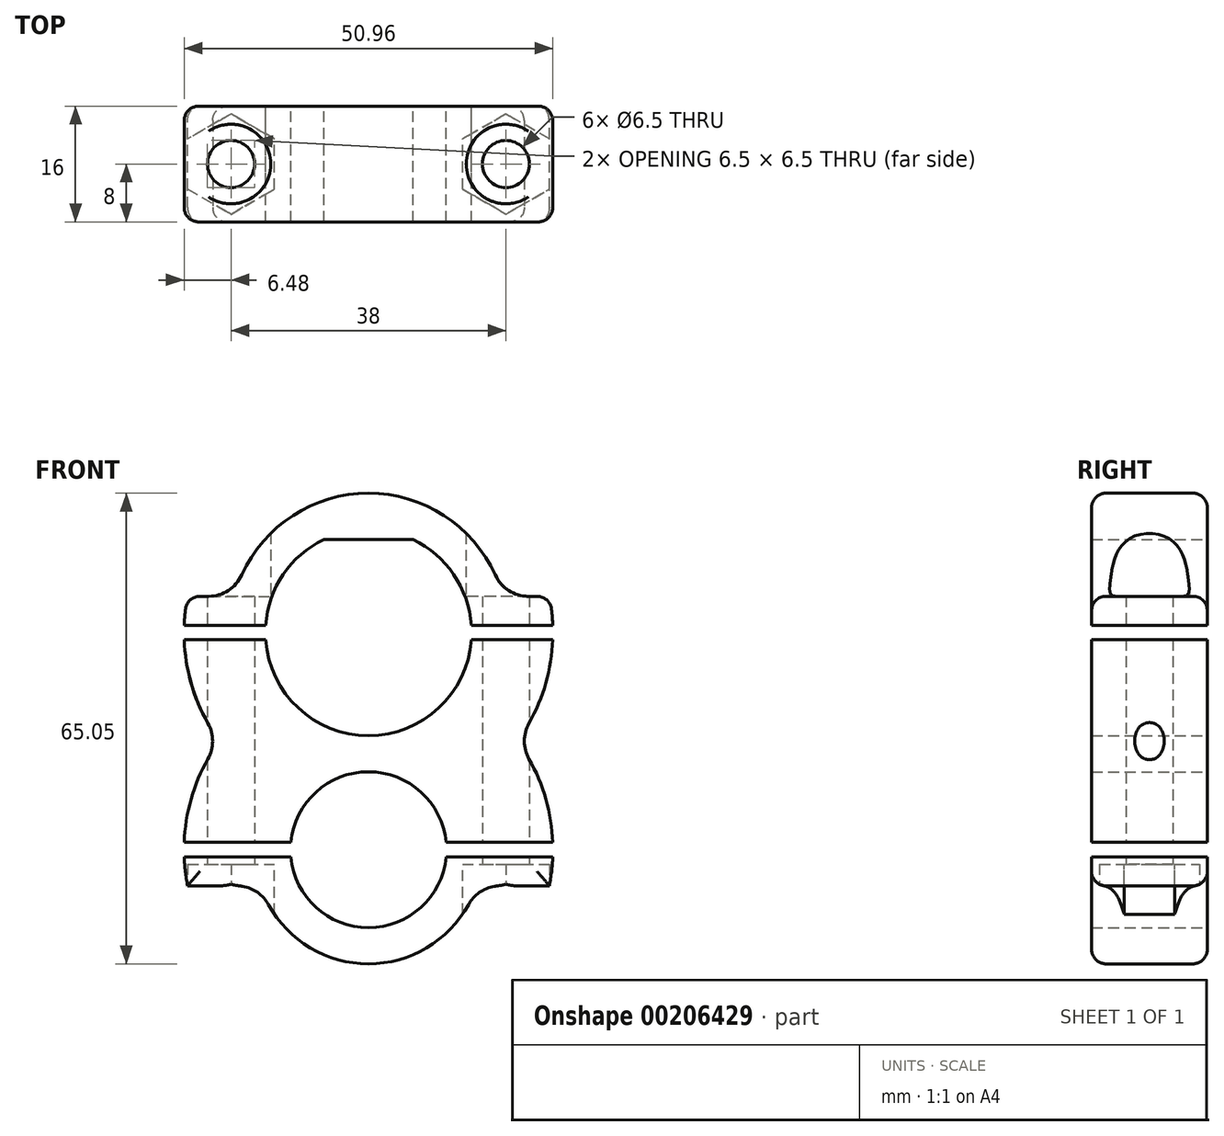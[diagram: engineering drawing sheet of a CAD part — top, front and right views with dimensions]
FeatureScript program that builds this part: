
annotation { "Feature Type Name" : "Feature", "Feature Type Description" : "" }
export const myFeature = defineFeature(function(context is Context, id is Id, definition is map)
    precondition{}
    {
        {
            var Q0;
            Q0=qCreatedBy(makeId("Front.planeOp"),FACE);
            var sketch = newSketch(context, id + "F0", { "sketchPlane" : qUnion([Q0])});
            skArc(sketch, "E0", {"start": v(-6.16, 12.85) * mm, "mid": v(-11.78, 8.01) * mm, "end": v(-14.21, 1) * mm});
            skArc(sketch, "E1", {"start": v(10.73, -29.02) * mm, "mid": v(0, -19.25) * mm, "end": v(-10.73, -29.02) * mm});
            skLineSegment(sketch, "E2", {"start": v(-6.16, 12.85) * mm, "end": v(6.16, 12.85) * mm});
            skLineSegment(sketch, "E3", {"start": v(-25, -35.02) * mm, "end": v(-14.96, -35.02) * mm});
            skLineSegment(sketch, "E4", {"start": v(-25, -25.02) * mm, "end": v(25, -25.02) * mm, "construction": true});
            skLineSegment(sketch, "E5", {"start": v(-25, -5) * mm, "end": v(25, -5) * mm, "construction": true});
            skLineSegment(sketch, "E6", {"start": v(-25, 5) * mm, "end": v(-18.59, 5) * mm});
            skArc(sketch, "E7", {"start": v(-25, 5) * mm, "mid": v(-25.32, 3) * mm, "end": v(-25.48, 1) * mm});
            skArc(sketch, "E8", {"start": v(25, -35.02) * mm, "mid": v(25.32, -33.03) * mm, "end": v(25.48, -31.03) * mm});
            skArc(sketch, "E9", {"start": v(20.6, -15.01) * mm, "mid": v(24.08, -8.37) * mm, "end": v(25.48, -1) * mm});
            skArc(sketch, "E10", {"start": v(-20.6, -15.01) * mm, "mid": v(-24.08, -21.66) * mm, "end": v(-25.48, -29.02) * mm});
            skLineSegment(sketch, "E11", {"start": v(-18.59, 5) * mm, "end": v(18.59, 5) * mm, "construction": true});
            skLineSegment(sketch, "E12", {"start": v(18.59, 5) * mm, "end": v(25, 5) * mm});
            skLineSegment(sketch, "E13", {"start": v(14.96, -35.02) * mm, "end": v(25, -35.02) * mm});
            skLineSegment(sketch, "E14", {"start": v(-14.96, -35.02) * mm, "end": v(14.96, -35.02) * mm, "construction": true});
            skArc(sketch, "E15", {"start": v(18.59, 5) * mm, "mid": v(0, 19.25) * mm, "end": v(-18.59, 5) * mm});
            skArc(sketch, "E16", {"start": v(-14.96, -35.02) * mm, "mid": v(0, -45.8) * mm, "end": v(14.96, -35.02) * mm});
            skLineSegment(sketch, "E17", {"start": v(-25.48, -31.03) * mm, "end": v(-10.73, -31.03) * mm});
            skLineSegment(sketch, "E18", {"start": v(-25.48, -29.02) * mm, "end": v(-10.73, -29.02) * mm});
            skLineSegment(sketch, "E19", {"start": v(-25.48, 1) * mm, "end": v(-14.21, 1) * mm});
            skLineSegment(sketch, "E20", {"start": v(25.48, -1) * mm, "end": v(14.21, -1) * mm});
            skLineSegment(sketch, "E21.trimOffspring", {"start": v(14.21, 1) * mm, "end": v(25.48, 1) * mm});
            skLineSegment(sketch, "E22.trimOffspring", {"start": v(-14.21, -1) * mm, "end": v(-25.48, -1) * mm});
            skLineSegment(sketch, "E23.trimOffspring", {"start": v(10.73, -29.02) * mm, "end": v(25.48, -29.02) * mm});
            skLineSegment(sketch, "E24.trimOffspring", {"start": v(10.73, -31.03) * mm, "end": v(25.48, -31.03) * mm});
            skArc(sketch, "E25.trimOffspring", {"start": v(-25.48, -1) * mm, "mid": v(-24.08, -8.37) * mm, "end": v(-20.6, -15.01) * mm});
            skArc(sketch, "E26.trimOffspring", {"start": v(25.48, 1) * mm, "mid": v(25.32, 3) * mm, "end": v(25, 5) * mm});
            skArc(sketch, "E27.trimOffspring", {"start": v(-25.48, -31.03) * mm, "mid": v(-25.32, -33.03) * mm, "end": v(-25, -35.02) * mm});
            skArc(sketch, "E28.trimOffspring", {"start": v(25.48, -29.02) * mm, "mid": v(24.08, -21.66) * mm, "end": v(20.6, -15.01) * mm});
            skArc(sketch, "E29.trimOffspring", {"start": v(-10.73, -31.03) * mm, "mid": v(0, -40.8) * mm, "end": v(10.73, -31.03) * mm});
            skArc(sketch, "E30.trimOffspring", {"start": v(-14.21, -1) * mm, "mid": v(0, -14.25) * mm, "end": v(14.21, -1) * mm});
            skArc(sketch, "E31.trimOffspring", {"start": v(14.21, 1) * mm, "mid": v(11.78, 8.01) * mm, "end": v(6.16, 12.85) * mm});
            skSolve(sketch);
        }
        {
            var Q0;
            Q0 = qSketchRegion(id + "F0", true);
            extrude(context, id + "F1", {"entities" : qUnion([Q0]), "endBound" : BoundingType.SYMMETRIC, "depth" : 16 * mm});
        }
        {
            var Q0;
            Q0=makeQuery(id+"F1.opExtrude","SWEPT_FACE",FACE,{"disambiguationData":[OSD([sQuery(id+"F0.wireOp",EDGE,"E3")])]});
            var sketch = newSketch(context, id + "F2", { "sketchPlane" : qUnion([Q0])});
            skCircle(sketch, "E32.cCircle", {"center": v(-19, 0) * mm, "radius": 6 * mm, "construction": true});
            skLineSegment(sketch, "E32.0", {"start": v(-19, 6.93) * mm, "end": v(-13, 3.46) * mm});
            skLineSegment(sketch, "E32.1", {"start": v(-13, 3.46) * mm, "end": v(-13, -3.46) * mm});
            skLineSegment(sketch, "E32.2", {"start": v(-13, -3.46) * mm, "end": v(-19, -6.93) * mm});
            skLineSegment(sketch, "E32.3", {"start": v(-19, -6.93) * mm, "end": v(-25, -3.46) * mm});
            skLineSegment(sketch, "E32.4", {"start": v(-25, -3.46) * mm, "end": v(-25, 3.46) * mm});
            skLineSegment(sketch, "E32.5", {"start": v(-25, 3.46) * mm, "end": v(-19, 6.93) * mm});
            skPoint(sketch, "E32.0.midPoint", {"position": v(-16, 5.2) * mm});
            skCircle(sketch, "E33.cCircle", {"center": v(19, 0) * mm, "radius": 6 * mm, "construction": true});
            skLineSegment(sketch, "E33.0", {"start": v(19, 6.93) * mm, "end": v(25, 3.46) * mm});
            skLineSegment(sketch, "E33.1", {"start": v(25, 3.46) * mm, "end": v(25, -3.46) * mm});
            skLineSegment(sketch, "E33.2", {"start": v(25, -3.46) * mm, "end": v(19, -6.93) * mm});
            skLineSegment(sketch, "E33.3", {"start": v(19, -6.93) * mm, "end": v(13, -3.46) * mm});
            skLineSegment(sketch, "E33.4", {"start": v(13, -3.46) * mm, "end": v(13, 3.46) * mm});
            skLineSegment(sketch, "E33.5", {"start": v(13, 3.46) * mm, "end": v(19, 6.93) * mm});
            skPoint(sketch, "E33.0.midPoint", {"position": v(22, 5.2) * mm});
            skCircle(sketch, "E34", {"center": v(-19, 0) * mm, "radius": 3.25 * mm});
            skCircle(sketch, "E35", {"center": v(19, 0) * mm, "radius": 3.25 * mm});
            skSolve(sketch);
        }
        {
            var Q0;
            {var subQ0=sQuery(id+"F2.wireOp",EDGE,"E34");var subQ1=makeQuery(id+"F1.opExtrude","SWEPT_EDGE",EDGE,{"disambiguationData":[OSD([sQuery(id+"F0.wireOp",EDGE,"E3"),sQuery(id+"F0.wireOp",EDGE,"E16")])]});var subQ2=makeQuery(id+"F2.imprint","INTERSECT",VERTEX,{"disambiguationData":[OD(0.0)],"derivedFrom":[subQ1,subQ0]});Q0=makeQuery(id+"F2.imprint","IMPRINT",FACE,{"disambiguationData":[TD([[makeQuery(id+"F2.imprint","IMPRINT",EDGE,{"disambiguationData":[TD([[subQ2,-1.0]])],"derivedFrom":subQ0}),1.0]])]});}
            var Q1;
            Q1=makeQuery(id+"F2.imprint","IMPRINT",FACE,{"disambiguationData":[TD([[makeQuery(id+"F2.imprint","IMPRINT",EDGE,{"derivedFrom":sQuery(id+"F2.wireOp",EDGE,"E35")}),1.0]])]});
            extrude(context, id + "F3", {"entities" : qUnion([Q0, Q1]), "operationType" : NewBodyOperationType.REMOVE, "endBound" : BoundingType.THROUGH_ALL, "oppositeDirection" : true, "depth" : 25 * mm});
        }
        {
            var Q0;
            Q0 = qSketchRegion(id + "F2", true);
            extrude(context, id + "F4", {"entities" : qUnion([Q0]), "operationType" : NewBodyOperationType.REMOVE, "depth" : 25 * mm});
        }
        {
            var Q0;
            Q0 = qSketchRegion(id + "F2", true);
            extrude(context, id + "F5", {"entities" : qUnion([Q0]), "operationType" : NewBodyOperationType.REMOVE, "oppositeDirection" : true, "depth" : 3 * mm});
        }
        {
            var Q0;
            Q0=makeQuery(id+"F1.opExtrude","SWEPT_FACE",FACE,{"disambiguationData":[OSD([sQuery(id+"F0.wireOp",EDGE,"E6")])]});
            var sketch = newSketch(context, id + "F6", { "sketchPlane" : qUnion([Q0])});
            skCircle(sketch, "E36", {"center": v(-19, 0) * mm, "radius": 5.5 * mm});
            skCircle(sketch, "E37", {"center": v(19, 0) * mm, "radius": 5.5 * mm});
            skSolve(sketch);
        }
        {
            var Q0;
            Q0 = qSketchRegion(id + "F6", true);
            extrude(context, id + "F7", {"entities" : qUnion([Q0]), "operationType" : NewBodyOperationType.REMOVE, "depth" : 25 * mm});
        }
        {
            var Q0;
            {var subQ0=sQuery(id+"F0.wireOp",EDGE,"E15");var subQ1=sQuery(id+"F0.wireOp",EDGE,"E6");Q0=makeQuery(id+"F3.boolean.opBoolean","SPLIT",EDGE,{"disambiguationData":[TD([makeQuery(id+"F1.opExtrude","CAP_FACE",FACE,{"disambiguationData":[OSD([sQuery(id+"F0.wireOp",EDGE,"E0"),sQuery(id+"F0.wireOp",EDGE,"E2"),subQ1,sQuery(id+"F0.wireOp",EDGE,"E7"),sQuery(id+"F0.wireOp",EDGE,"E12"),subQ0,sQuery(id+"F0.wireOp",EDGE,"E19"),sQuery(id+"F0.wireOp",EDGE,"E21.trimOffspring"),sQuery(id+"F0.wireOp",EDGE,"E26.trimOffspring"),sQuery(id+"F0.wireOp",EDGE,"E31.trimOffspring")])],"isStart":false})])],"derivedFrom":makeQuery(id+"F1.opExtrude","SWEPT_EDGE",EDGE,{"disambiguationData":[OSD([subQ1,subQ0])]})});}
            var Q1;
            {var subQ0=sQuery(id+"F0.wireOp",EDGE,"E15");var subQ1=sQuery(id+"F0.wireOp",EDGE,"E6");Q1=makeQuery(id+"F3.boolean.opBoolean","SPLIT",EDGE,{"disambiguationData":[TD([makeQuery(id+"F1.opExtrude","CAP_FACE",FACE,{"disambiguationData":[OSD([sQuery(id+"F0.wireOp",EDGE,"E0"),sQuery(id+"F0.wireOp",EDGE,"E2"),subQ1,sQuery(id+"F0.wireOp",EDGE,"E7"),sQuery(id+"F0.wireOp",EDGE,"E12"),subQ0,sQuery(id+"F0.wireOp",EDGE,"E19"),sQuery(id+"F0.wireOp",EDGE,"E21.trimOffspring"),sQuery(id+"F0.wireOp",EDGE,"E26.trimOffspring"),sQuery(id+"F0.wireOp",EDGE,"E31.trimOffspring")])],"isStart":true})])],"derivedFrom":makeQuery(id+"F1.opExtrude","SWEPT_EDGE",EDGE,{"disambiguationData":[OSD([subQ1,subQ0])]})});}
            var Q2;
            {var subQ0=sQuery(id+"F0.wireOp",EDGE,"E15");var subQ1=sQuery(id+"F0.wireOp",EDGE,"E12");Q2=makeQuery(id+"F3.boolean.opBoolean","SPLIT",EDGE,{"disambiguationData":[TD([makeQuery(id+"F1.opExtrude","CAP_FACE",FACE,{"disambiguationData":[OSD([sQuery(id+"F0.wireOp",EDGE,"E0"),sQuery(id+"F0.wireOp",EDGE,"E2"),sQuery(id+"F0.wireOp",EDGE,"E6"),sQuery(id+"F0.wireOp",EDGE,"E7"),subQ1,subQ0,sQuery(id+"F0.wireOp",EDGE,"E19"),sQuery(id+"F0.wireOp",EDGE,"E21.trimOffspring"),sQuery(id+"F0.wireOp",EDGE,"E26.trimOffspring"),sQuery(id+"F0.wireOp",EDGE,"E31.trimOffspring")])],"isStart":false})])],"derivedFrom":makeQuery(id+"F1.opExtrude","SWEPT_EDGE",EDGE,{"disambiguationData":[OSD([subQ1,subQ0])]})});}
            var Q3;
            {var subQ0=sQuery(id+"F0.wireOp",EDGE,"E15");var subQ1=sQuery(id+"F0.wireOp",EDGE,"E12");Q3=makeQuery(id+"F3.boolean.opBoolean","SPLIT",EDGE,{"disambiguationData":[TD([makeQuery(id+"F1.opExtrude","CAP_FACE",FACE,{"disambiguationData":[OSD([sQuery(id+"F0.wireOp",EDGE,"E0"),sQuery(id+"F0.wireOp",EDGE,"E2"),sQuery(id+"F0.wireOp",EDGE,"E6"),sQuery(id+"F0.wireOp",EDGE,"E7"),subQ1,subQ0,sQuery(id+"F0.wireOp",EDGE,"E19"),sQuery(id+"F0.wireOp",EDGE,"E21.trimOffspring"),sQuery(id+"F0.wireOp",EDGE,"E26.trimOffspring"),sQuery(id+"F0.wireOp",EDGE,"E31.trimOffspring")])],"isStart":true})])],"derivedFrom":makeQuery(id+"F1.opExtrude","SWEPT_EDGE",EDGE,{"disambiguationData":[OSD([subQ1,subQ0])]})});}
            var Q4;
            {var subQ0=sQuery(id+"F2.wireOp",EDGE,"E33.5");var subQ1=sQuery(id+"F0.wireOp",EDGE,"E13");var subQ2=sQuery(id+"F0.wireOp",EDGE,"E16");Q4=makeQuery(id+"F4.boolean.opBoolean","SPLIT",EDGE,{"disambiguationData":[TD([makeQuery(id+"F4.opExtrude","SWEPT_FACE",FACE,{"disambiguationData":[OSD([subQ0])]})])],"derivedFrom":makeQuery(id+"F1.opExtrude","SWEPT_EDGE",EDGE,{"disambiguationData":[OSD([subQ1,subQ2])]})});}
            var Q5;
            {var subQ0=sQuery(id+"F2.wireOp",EDGE,"E33.3");var subQ1=sQuery(id+"F0.wireOp",EDGE,"E13");var subQ2=sQuery(id+"F0.wireOp",EDGE,"E16");Q5=makeQuery(id+"F4.boolean.opBoolean","SPLIT",EDGE,{"disambiguationData":[TD([makeQuery(id+"F4.opExtrude","SWEPT_FACE",FACE,{"disambiguationData":[OSD([subQ0])]})])],"derivedFrom":makeQuery(id+"F1.opExtrude","SWEPT_EDGE",EDGE,{"disambiguationData":[OSD([subQ1,subQ2])]})});}
            var Q6;
            {var subQ0=sQuery(id+"F2.wireOp",EDGE,"E32.0");var subQ1=sQuery(id+"F0.wireOp",EDGE,"E16");var subQ2=sQuery(id+"F0.wireOp",EDGE,"E3");Q6=makeQuery(id+"F4.boolean.opBoolean","SPLIT",EDGE,{"disambiguationData":[TD([makeQuery(id+"F4.opExtrude","SWEPT_FACE",FACE,{"disambiguationData":[OSD([subQ0])]})])],"derivedFrom":makeQuery(id+"F1.opExtrude","SWEPT_EDGE",EDGE,{"disambiguationData":[OSD([subQ2,subQ1])]})});}
            var Q7;
            {var subQ0=sQuery(id+"F2.wireOp",EDGE,"E32.2");var subQ1=sQuery(id+"F0.wireOp",EDGE,"E16");var subQ2=sQuery(id+"F0.wireOp",EDGE,"E3");Q7=makeQuery(id+"F4.boolean.opBoolean","SPLIT",EDGE,{"disambiguationData":[TD([makeQuery(id+"F4.opExtrude","SWEPT_FACE",FACE,{"disambiguationData":[OSD([subQ0])]})])],"derivedFrom":makeQuery(id+"F1.opExtrude","SWEPT_EDGE",EDGE,{"disambiguationData":[OSD([subQ2,subQ1])]})});}
            var Q8;
            {var subQ0=sQuery(id+"F0.wireOp",EDGE,"E28.trimOffspring");var subQ1=sQuery(id+"F0.wireOp",EDGE,"E9");Q8=makeQuery(id+"F3.boolean.opBoolean","SPLIT",EDGE,{"disambiguationData":[TD([makeQuery(id+"F1.opExtrude","CAP_FACE",FACE,{"disambiguationData":[OSD([sQuery(id+"F0.wireOp",EDGE,"E1"),subQ1,sQuery(id+"F0.wireOp",EDGE,"E10"),sQuery(id+"F0.wireOp",EDGE,"E18"),sQuery(id+"F0.wireOp",EDGE,"E20"),sQuery(id+"F0.wireOp",EDGE,"E22.trimOffspring"),sQuery(id+"F0.wireOp",EDGE,"E23.trimOffspring"),sQuery(id+"F0.wireOp",EDGE,"E25.trimOffspring"),subQ0,sQuery(id+"F0.wireOp",EDGE,"E30.trimOffspring")])],"isStart":true})])],"derivedFrom":makeQuery(id+"F1.opExtrude","SWEPT_EDGE",EDGE,{"disambiguationData":[OSD([subQ1,subQ0])]})});}
            var Q9;
            {var subQ0=sQuery(id+"F0.wireOp",EDGE,"E28.trimOffspring");var subQ1=sQuery(id+"F0.wireOp",EDGE,"E9");Q9=makeQuery(id+"F3.boolean.opBoolean","SPLIT",EDGE,{"disambiguationData":[TD([makeQuery(id+"F1.opExtrude","CAP_FACE",FACE,{"disambiguationData":[OSD([sQuery(id+"F0.wireOp",EDGE,"E1"),subQ1,sQuery(id+"F0.wireOp",EDGE,"E10"),sQuery(id+"F0.wireOp",EDGE,"E18"),sQuery(id+"F0.wireOp",EDGE,"E20"),sQuery(id+"F0.wireOp",EDGE,"E22.trimOffspring"),sQuery(id+"F0.wireOp",EDGE,"E23.trimOffspring"),sQuery(id+"F0.wireOp",EDGE,"E25.trimOffspring"),subQ0,sQuery(id+"F0.wireOp",EDGE,"E30.trimOffspring")])],"isStart":false})])],"derivedFrom":makeQuery(id+"F1.opExtrude","SWEPT_EDGE",EDGE,{"disambiguationData":[OSD([subQ1,subQ0])]})});}
            var Q10;
            {var subQ0=sQuery(id+"F0.wireOp",EDGE,"E25.trimOffspring");var subQ1=sQuery(id+"F0.wireOp",EDGE,"E10");Q10=makeQuery(id+"F3.boolean.opBoolean","SPLIT",EDGE,{"disambiguationData":[TD([makeQuery(id+"F1.opExtrude","CAP_FACE",FACE,{"disambiguationData":[OSD([sQuery(id+"F0.wireOp",EDGE,"E1"),sQuery(id+"F0.wireOp",EDGE,"E9"),subQ1,sQuery(id+"F0.wireOp",EDGE,"E18"),sQuery(id+"F0.wireOp",EDGE,"E20"),sQuery(id+"F0.wireOp",EDGE,"E22.trimOffspring"),sQuery(id+"F0.wireOp",EDGE,"E23.trimOffspring"),subQ0,sQuery(id+"F0.wireOp",EDGE,"E28.trimOffspring"),sQuery(id+"F0.wireOp",EDGE,"E30.trimOffspring")])],"isStart":false})])],"derivedFrom":makeQuery(id+"F1.opExtrude","SWEPT_EDGE",EDGE,{"disambiguationData":[OSD([subQ1,subQ0])]})});}
            var Q11;
            {var subQ0=sQuery(id+"F0.wireOp",EDGE,"E25.trimOffspring");var subQ1=sQuery(id+"F0.wireOp",EDGE,"E10");Q11=makeQuery(id+"F3.boolean.opBoolean","SPLIT",EDGE,{"disambiguationData":[TD([makeQuery(id+"F1.opExtrude","CAP_FACE",FACE,{"disambiguationData":[OSD([sQuery(id+"F0.wireOp",EDGE,"E1"),sQuery(id+"F0.wireOp",EDGE,"E9"),subQ1,sQuery(id+"F0.wireOp",EDGE,"E18"),sQuery(id+"F0.wireOp",EDGE,"E20"),sQuery(id+"F0.wireOp",EDGE,"E22.trimOffspring"),sQuery(id+"F0.wireOp",EDGE,"E23.trimOffspring"),subQ0,sQuery(id+"F0.wireOp",EDGE,"E28.trimOffspring"),sQuery(id+"F0.wireOp",EDGE,"E30.trimOffspring")])],"isStart":true})])],"derivedFrom":makeQuery(id+"F1.opExtrude","SWEPT_EDGE",EDGE,{"disambiguationData":[OSD([subQ1,subQ0])]})});}
            fillet(context, id + "F8", {"entities" : qUnion([Q0, Q1, Q2, Q3, Q4, Q5, Q6, Q7, Q8, Q9, Q10, Q11]), "radius" : 5 * mm, "tangentPropagation" : true, "allowEdgeOverflow" : false});
        }
        {
            var Q0;
            Q0=makeQuery(id+"F1.opExtrude","CAP_EDGE",EDGE,{"disambiguationData":[OSD([sQuery(id+"F0.wireOp",EDGE,"E15")])],"isStart":false});
            var Q1;
            Q1=makeQuery(id+"F1.opExtrude","CAP_EDGE",EDGE,{"disambiguationData":[OSD([sQuery(id+"F0.wireOp",EDGE,"E16")])],"isStart":false});
            var Q2;
            Q2=makeQuery(id+"F1.opExtrude","CAP_EDGE",EDGE,{"disambiguationData":[OSD([sQuery(id+"F0.wireOp",EDGE,"E28.trimOffspring")])],"isStart":false});
            var Q3;
            Q3=makeQuery(id+"F1.opExtrude","CAP_EDGE",EDGE,{"disambiguationData":[OSD([sQuery(id+"F0.wireOp",EDGE,"E9")])],"isStart":false});
            var Q4;
            Q4=makeQuery(id+"F1.opExtrude","CAP_EDGE",EDGE,{"disambiguationData":[OSD([sQuery(id+"F0.wireOp",EDGE,"E10")])],"isStart":false});
            var Q5;
            Q5=makeQuery(id+"F1.opExtrude","CAP_EDGE",EDGE,{"disambiguationData":[OSD([sQuery(id+"F0.wireOp",EDGE,"E25.trimOffspring")])],"isStart":false});
            var Q6;
            Q6=makeQuery(id+"F1.opExtrude","CAP_EDGE",EDGE,{"disambiguationData":[OSD([sQuery(id+"F0.wireOp",EDGE,"E26.trimOffspring")])],"isStart":false});
            var Q7;
            Q7=makeQuery(id+"F1.opExtrude","CAP_EDGE",EDGE,{"disambiguationData":[OSD([sQuery(id+"F0.wireOp",EDGE,"E7")])],"isStart":false});
            var Q8;
            Q8=makeQuery(id+"F1.opExtrude","CAP_EDGE",EDGE,{"disambiguationData":[OSD([sQuery(id+"F0.wireOp",EDGE,"E27.trimOffspring")])],"isStart":false});
            var Q9;
            Q9=makeQuery(id+"F1.opExtrude","CAP_EDGE",EDGE,{"disambiguationData":[OSD([sQuery(id+"F0.wireOp",EDGE,"E8")])],"isStart":false});
            var Q10;
            Q10=makeQuery(id+"F1.opExtrude","CAP_EDGE",EDGE,{"disambiguationData":[OSD([sQuery(id+"F0.wireOp",EDGE,"E13")])],"isStart":false});
            var Q11;
            {var subQ0=sQuery(id+"F0.wireOp",EDGE,"E16");var subQ1=sQuery(id+"F0.wireOp",EDGE,"E13");var subQ2=makeQuery(id+"F1.opExtrude","CAP_FACE",FACE,{"disambiguationData":[OSD([sQuery(id+"F0.wireOp",EDGE,"E3"),sQuery(id+"F0.wireOp",EDGE,"E8"),subQ1,subQ0,sQuery(id+"F0.wireOp",EDGE,"E17"),sQuery(id+"F0.wireOp",EDGE,"E24.trimOffspring"),sQuery(id+"F0.wireOp",EDGE,"E27.trimOffspring"),sQuery(id+"F0.wireOp",EDGE,"E29.trimOffspring")])],"isStart":false});var subQ3=sQuery(id+"F2.wireOp",EDGE,"E33.5");Q11=makeQuery(id+"F8.opFillet","BLEND_EDGE",EDGE,{"blendedFrom":[makeQuery(id+"F4.boolean.opBoolean","SPLIT",EDGE,{"disambiguationData":[TD([makeQuery(id+"F4.opExtrude","SWEPT_FACE",FACE,{"disambiguationData":[OSD([subQ3])]})])],"derivedFrom":makeQuery(id+"F1.opExtrude","SWEPT_EDGE",EDGE,{"disambiguationData":[OSD([subQ1,subQ0])]})}),subQ2],"blendedInto":[subQ2]});}
            var Q12;
            {var subQ0=sQuery(id+"F0.wireOp",EDGE,"E16");var subQ1=sQuery(id+"F0.wireOp",EDGE,"E3");var subQ2=makeQuery(id+"F1.opExtrude","CAP_FACE",FACE,{"disambiguationData":[OSD([subQ1,sQuery(id+"F0.wireOp",EDGE,"E8"),sQuery(id+"F0.wireOp",EDGE,"E13"),subQ0,sQuery(id+"F0.wireOp",EDGE,"E17"),sQuery(id+"F0.wireOp",EDGE,"E24.trimOffspring"),sQuery(id+"F0.wireOp",EDGE,"E27.trimOffspring"),sQuery(id+"F0.wireOp",EDGE,"E29.trimOffspring")])],"isStart":false});var subQ3=sQuery(id+"F2.wireOp",EDGE,"E32.0");Q12=makeQuery(id+"F8.opFillet","BLEND_EDGE",EDGE,{"blendedFrom":[makeQuery(id+"F4.boolean.opBoolean","SPLIT",EDGE,{"disambiguationData":[TD([makeQuery(id+"F4.opExtrude","SWEPT_FACE",FACE,{"disambiguationData":[OSD([subQ3])]})])],"derivedFrom":makeQuery(id+"F1.opExtrude","SWEPT_EDGE",EDGE,{"disambiguationData":[OSD([subQ1,subQ0])]})}),subQ2],"blendedInto":[subQ2]});}
            var Q13;
            Q13=makeQuery(id+"F1.opExtrude","CAP_EDGE",EDGE,{"disambiguationData":[OSD([sQuery(id+"F0.wireOp",EDGE,"E3")])],"isStart":false});
            var Q14;
            {var subQ0=sQuery(id+"F0.wireOp",EDGE,"E15");var subQ1=sQuery(id+"F0.wireOp",EDGE,"E6");var subQ2=makeQuery(id+"F1.opExtrude","CAP_FACE",FACE,{"disambiguationData":[OSD([sQuery(id+"F0.wireOp",EDGE,"E0"),sQuery(id+"F0.wireOp",EDGE,"E2"),subQ1,sQuery(id+"F0.wireOp",EDGE,"E7"),sQuery(id+"F0.wireOp",EDGE,"E12"),subQ0,sQuery(id+"F0.wireOp",EDGE,"E19"),sQuery(id+"F0.wireOp",EDGE,"E21.trimOffspring"),sQuery(id+"F0.wireOp",EDGE,"E26.trimOffspring"),sQuery(id+"F0.wireOp",EDGE,"E31.trimOffspring")])],"isStart":false});Q14=makeQuery(id+"F8.opFillet","BLEND_EDGE",EDGE,{"blendedFrom":[makeQuery(id+"F3.boolean.opBoolean","SPLIT",EDGE,{"disambiguationData":[TD([subQ2])],"derivedFrom":makeQuery(id+"F1.opExtrude","SWEPT_EDGE",EDGE,{"disambiguationData":[OSD([subQ1,subQ0])]})}),subQ2],"blendedInto":[subQ2]});}
            var Q15;
            Q15=makeQuery(id+"F1.opExtrude","CAP_EDGE",EDGE,{"disambiguationData":[OSD([sQuery(id+"F0.wireOp",EDGE,"E6")])],"isStart":false});
            var Q16;
            {var subQ0=sQuery(id+"F0.wireOp",EDGE,"E15");var subQ1=sQuery(id+"F0.wireOp",EDGE,"E12");var subQ2=makeQuery(id+"F1.opExtrude","CAP_FACE",FACE,{"disambiguationData":[OSD([sQuery(id+"F0.wireOp",EDGE,"E0"),sQuery(id+"F0.wireOp",EDGE,"E2"),sQuery(id+"F0.wireOp",EDGE,"E6"),sQuery(id+"F0.wireOp",EDGE,"E7"),subQ1,subQ0,sQuery(id+"F0.wireOp",EDGE,"E19"),sQuery(id+"F0.wireOp",EDGE,"E21.trimOffspring"),sQuery(id+"F0.wireOp",EDGE,"E26.trimOffspring"),sQuery(id+"F0.wireOp",EDGE,"E31.trimOffspring")])],"isStart":false});Q16=makeQuery(id+"F8.opFillet","BLEND_EDGE",EDGE,{"blendedFrom":[makeQuery(id+"F3.boolean.opBoolean","SPLIT",EDGE,{"disambiguationData":[TD([subQ2])],"derivedFrom":makeQuery(id+"F1.opExtrude","SWEPT_EDGE",EDGE,{"disambiguationData":[OSD([subQ1,subQ0])]})}),subQ2],"blendedInto":[subQ2]});}
            var Q17;
            Q17=makeQuery(id+"F1.opExtrude","CAP_EDGE",EDGE,{"disambiguationData":[OSD([sQuery(id+"F0.wireOp",EDGE,"E12")])],"isStart":false});
            var Q18;
            Q18=makeQuery(id+"F1.opExtrude","CAP_EDGE",EDGE,{"disambiguationData":[OSD([sQuery(id+"F0.wireOp",EDGE,"E12")])],"isStart":true});
            var Q19;
            {var subQ0=sQuery(id+"F0.wireOp",EDGE,"E15");var subQ1=sQuery(id+"F0.wireOp",EDGE,"E12");var subQ2=makeQuery(id+"F1.opExtrude","CAP_FACE",FACE,{"disambiguationData":[OSD([sQuery(id+"F0.wireOp",EDGE,"E0"),sQuery(id+"F0.wireOp",EDGE,"E2"),sQuery(id+"F0.wireOp",EDGE,"E6"),sQuery(id+"F0.wireOp",EDGE,"E7"),subQ1,subQ0,sQuery(id+"F0.wireOp",EDGE,"E19"),sQuery(id+"F0.wireOp",EDGE,"E21.trimOffspring"),sQuery(id+"F0.wireOp",EDGE,"E26.trimOffspring"),sQuery(id+"F0.wireOp",EDGE,"E31.trimOffspring")])],"isStart":true});Q19=makeQuery(id+"F8.opFillet","BLEND_EDGE",EDGE,{"blendedFrom":[makeQuery(id+"F3.boolean.opBoolean","SPLIT",EDGE,{"disambiguationData":[TD([subQ2])],"derivedFrom":makeQuery(id+"F1.opExtrude","SWEPT_EDGE",EDGE,{"disambiguationData":[OSD([subQ1,subQ0])]})}),subQ2],"blendedInto":[subQ2]});}
            var Q20;
            Q20=makeQuery(id+"F1.opExtrude","CAP_EDGE",EDGE,{"disambiguationData":[OSD([sQuery(id+"F0.wireOp",EDGE,"E15")])],"isStart":true});
            var Q21;
            {var subQ0=sQuery(id+"F0.wireOp",EDGE,"E15");var subQ1=sQuery(id+"F0.wireOp",EDGE,"E6");var subQ2=makeQuery(id+"F1.opExtrude","CAP_FACE",FACE,{"disambiguationData":[OSD([sQuery(id+"F0.wireOp",EDGE,"E0"),sQuery(id+"F0.wireOp",EDGE,"E2"),subQ1,sQuery(id+"F0.wireOp",EDGE,"E7"),sQuery(id+"F0.wireOp",EDGE,"E12"),subQ0,sQuery(id+"F0.wireOp",EDGE,"E19"),sQuery(id+"F0.wireOp",EDGE,"E21.trimOffspring"),sQuery(id+"F0.wireOp",EDGE,"E26.trimOffspring"),sQuery(id+"F0.wireOp",EDGE,"E31.trimOffspring")])],"isStart":true});Q21=makeQuery(id+"F8.opFillet","BLEND_EDGE",EDGE,{"blendedFrom":[makeQuery(id+"F3.boolean.opBoolean","SPLIT",EDGE,{"disambiguationData":[TD([subQ2])],"derivedFrom":makeQuery(id+"F1.opExtrude","SWEPT_EDGE",EDGE,{"disambiguationData":[OSD([subQ1,subQ0])]})}),subQ2],"blendedInto":[subQ2]});}
            var Q22;
            Q22=makeQuery(id+"F1.opExtrude","CAP_EDGE",EDGE,{"disambiguationData":[OSD([sQuery(id+"F0.wireOp",EDGE,"E6")])],"isStart":true});
            var Q23;
            Q23=makeQuery(id+"F1.opExtrude","CAP_EDGE",EDGE,{"disambiguationData":[OSD([sQuery(id+"F0.wireOp",EDGE,"E25.trimOffspring")])],"isStart":true});
            var Q24;
            Q24=makeQuery(id+"F1.opExtrude","CAP_EDGE",EDGE,{"disambiguationData":[OSD([sQuery(id+"F0.wireOp",EDGE,"E10")])],"isStart":true});
            var Q25;
            Q25=makeQuery(id+"F1.opExtrude","CAP_EDGE",EDGE,{"disambiguationData":[OSD([sQuery(id+"F0.wireOp",EDGE,"E28.trimOffspring")])],"isStart":true});
            var Q26;
            Q26=makeQuery(id+"F1.opExtrude","CAP_EDGE",EDGE,{"disambiguationData":[OSD([sQuery(id+"F0.wireOp",EDGE,"E9")])],"isStart":true});
            var Q27;
            Q27=makeQuery(id+"F1.opExtrude","CAP_EDGE",EDGE,{"disambiguationData":[OSD([sQuery(id+"F0.wireOp",EDGE,"E13")])],"isStart":true});
            var Q28;
            {var subQ0=sQuery(id+"F0.wireOp",EDGE,"E16");var subQ1=sQuery(id+"F0.wireOp",EDGE,"E13");var subQ2=makeQuery(id+"F1.opExtrude","CAP_FACE",FACE,{"disambiguationData":[OSD([sQuery(id+"F0.wireOp",EDGE,"E3"),sQuery(id+"F0.wireOp",EDGE,"E8"),subQ1,subQ0,sQuery(id+"F0.wireOp",EDGE,"E17"),sQuery(id+"F0.wireOp",EDGE,"E24.trimOffspring"),sQuery(id+"F0.wireOp",EDGE,"E27.trimOffspring"),sQuery(id+"F0.wireOp",EDGE,"E29.trimOffspring")])],"isStart":true});var subQ3=sQuery(id+"F2.wireOp",EDGE,"E33.3");Q28=makeQuery(id+"F8.opFillet","BLEND_EDGE",EDGE,{"blendedFrom":[makeQuery(id+"F4.boolean.opBoolean","SPLIT",EDGE,{"disambiguationData":[TD([makeQuery(id+"F4.opExtrude","SWEPT_FACE",FACE,{"disambiguationData":[OSD([subQ3])]})])],"derivedFrom":makeQuery(id+"F1.opExtrude","SWEPT_EDGE",EDGE,{"disambiguationData":[OSD([subQ1,subQ0])]})}),subQ2],"blendedInto":[subQ2]});}
            var Q29;
            Q29=makeQuery(id+"F1.opExtrude","CAP_EDGE",EDGE,{"disambiguationData":[OSD([sQuery(id+"F0.wireOp",EDGE,"E16")])],"isStart":true});
            var Q30;
            {var subQ0=sQuery(id+"F0.wireOp",EDGE,"E16");var subQ1=sQuery(id+"F0.wireOp",EDGE,"E3");var subQ2=makeQuery(id+"F1.opExtrude","CAP_FACE",FACE,{"disambiguationData":[OSD([subQ1,sQuery(id+"F0.wireOp",EDGE,"E8"),sQuery(id+"F0.wireOp",EDGE,"E13"),subQ0,sQuery(id+"F0.wireOp",EDGE,"E17"),sQuery(id+"F0.wireOp",EDGE,"E24.trimOffspring"),sQuery(id+"F0.wireOp",EDGE,"E27.trimOffspring"),sQuery(id+"F0.wireOp",EDGE,"E29.trimOffspring")])],"isStart":true});var subQ3=sQuery(id+"F2.wireOp",EDGE,"E32.2");Q30=makeQuery(id+"F8.opFillet","BLEND_EDGE",EDGE,{"blendedFrom":[makeQuery(id+"F4.boolean.opBoolean","SPLIT",EDGE,{"disambiguationData":[TD([makeQuery(id+"F4.opExtrude","SWEPT_FACE",FACE,{"disambiguationData":[OSD([subQ3])]})])],"derivedFrom":makeQuery(id+"F1.opExtrude","SWEPT_EDGE",EDGE,{"disambiguationData":[OSD([subQ1,subQ0])]})}),subQ2],"blendedInto":[subQ2]});}
            var Q31;
            Q31=makeQuery(id+"F1.opExtrude","CAP_EDGE",EDGE,{"disambiguationData":[OSD([sQuery(id+"F0.wireOp",EDGE,"E3")])],"isStart":true});
            var Q32;
            Q32=makeQuery(id+"F1.opExtrude","CAP_EDGE",EDGE,{"disambiguationData":[OSD([sQuery(id+"F0.wireOp",EDGE,"E27.trimOffspring")])],"isStart":true});
            var Q33;
            Q33=makeQuery(id+"F1.opExtrude","CAP_EDGE",EDGE,{"disambiguationData":[OSD([sQuery(id+"F0.wireOp",EDGE,"E8")])],"isStart":true});
            var Q34;
            Q34=makeQuery(id+"F1.opExtrude","CAP_EDGE",EDGE,{"disambiguationData":[OSD([sQuery(id+"F0.wireOp",EDGE,"E26.trimOffspring")])],"isStart":true});
            var Q35;
            Q35=makeQuery(id+"F1.opExtrude","CAP_EDGE",EDGE,{"disambiguationData":[OSD([sQuery(id+"F0.wireOp",EDGE,"E7")])],"isStart":true});
            var Q36;
            Q36=makeQuery(id+"F1.opExtrude","SWEPT_EDGE",EDGE,{"disambiguationData":[OSD([sQuery(id+"F0.wireOp",EDGE,"E6"),sQuery(id+"F0.wireOp",EDGE,"E7")])]});
            var Q37;
            Q37=makeQuery(id+"F1.opExtrude","SWEPT_EDGE",EDGE,{"disambiguationData":[OSD([sQuery(id+"F0.wireOp",EDGE,"E12"),sQuery(id+"F0.wireOp",EDGE,"E26.trimOffspring")])]});
            fillet(context, id + "F9", {"entities" : qUnion([Q0, Q1, Q2, Q3, Q4, Q5, Q6, Q7, Q8, Q9, Q10, Q11, Q12, Q13, Q14, Q15, Q16, Q17, Q18, Q19, Q20, Q21, Q22, Q23, Q24, Q25, Q26, Q27, Q28, Q29, Q30, Q31, Q32, Q33, Q34, Q35, Q36, Q37]), "radius" : 2 * mm, "tangentPropagation" : true, "allowEdgeOverflow" : false});
        }
    });
